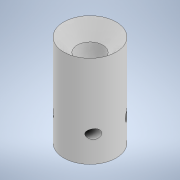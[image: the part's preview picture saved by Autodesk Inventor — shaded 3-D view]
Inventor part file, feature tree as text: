
AUTODESK INVENTOR PART (.ipt)
format: ipt  version: 2020 (Build 240168000, 168)  size: 157,184 bytes
history: native  units: in
note: dims shown in document units (in); Inventor stores cm internally (conversion verified against a paired STEP export)
features: sketch x3, hole x2, revolve x1, mirror x1
ambient origin geometry x8: Origin, YZ Plane, XZ Plane, XY Plane, X Axis, Y Axis, Z Axis, Center Point
bodies: Solid1 (feature_tree)
feature tree (7):
  revolve  "Revolution1"  [1 undecoded]
  hole  "Hole2"  [1 undecoded]
  hole  "Hole3"  [1 undecoded]
  mirror  "Mirror1"
  sketch  "Sketch1"  dims[d0=0.245in d1=0.0in]
  sketch  "Sketch3"  dims[d2=1.5in d3=90.0deg]
  sketch  "Sketch4"  dims[d4=0.03in d5=0.325in d6=165.0deg d7=0.5in d8=90.0deg d18=45.0deg d19=0.211in d20=0.25in d21=0.375in d22=0.25in d23=0.5635in d24=0.25in d25=0.0in d28=0.188in d29=0.5in d30=0.188in d31=0.5in d32=90.0deg d33=0.177in d34=0.328in d35=0.119in d36=0.25in d37=0.5635in d38=0.484in d39=0.0in d47=0.3779in]
note: 3 required parameter values undecoded (feature->parameter linkage not recoverable at this tier; creation-order binding heuristic only, values carry confidence <= 0.55)